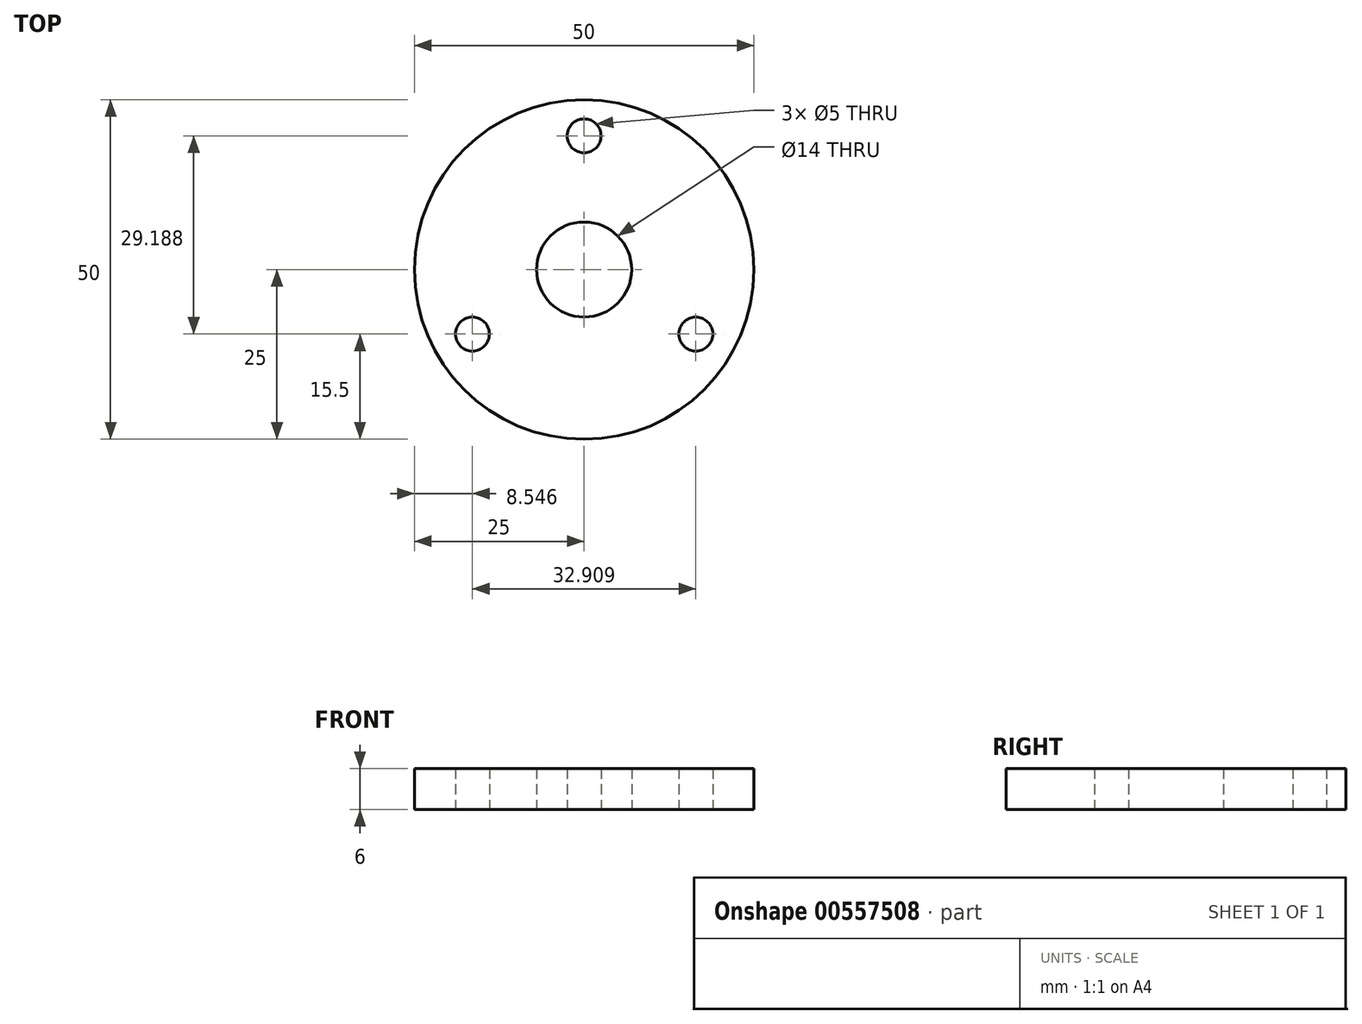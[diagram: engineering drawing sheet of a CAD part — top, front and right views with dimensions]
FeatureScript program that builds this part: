
annotation { "Feature Type Name" : "Feature", "Feature Type Description" : "" }
export const myFeature = defineFeature(function(context is Context, id is Id, definition is map)
    precondition{}
    {
        {
            var Q0;
            Q0=qCreatedBy(makeId("Top.planeOp"),FACE);
            var sketch = newSketch(context, id + "F0", { "sketchPlane" : qUnion([Q0])});
            skCircle(sketch, "E0", {"center": v(0, 0) * mm, "radius": 25 * mm});
            skCircle(sketch, "E1", {"center": v(0, 0) * mm, "radius": 7 * mm});
            skCircle(sketch, "E2", {"center": v(0, 19.69) * mm, "radius": 2.5 * mm});
            skCircle(sketch, "E3", {"center": v(-16.45, -9.5) * mm, "radius": 2.5 * mm});
            skCircle(sketch, "E4", {"center": v(16.45, -9.5) * mm, "radius": 2.5 * mm});
            skSolve(sketch);
        }
        {
            var Q0;
            Q0 = qSketchRegion(id + "F0", true);
            extrude(context, id + "F1", {"entities" : qUnion([Q0]), "depth" : 6 * mm, "offsetDistance" : 25 * mm});
        }
    });
